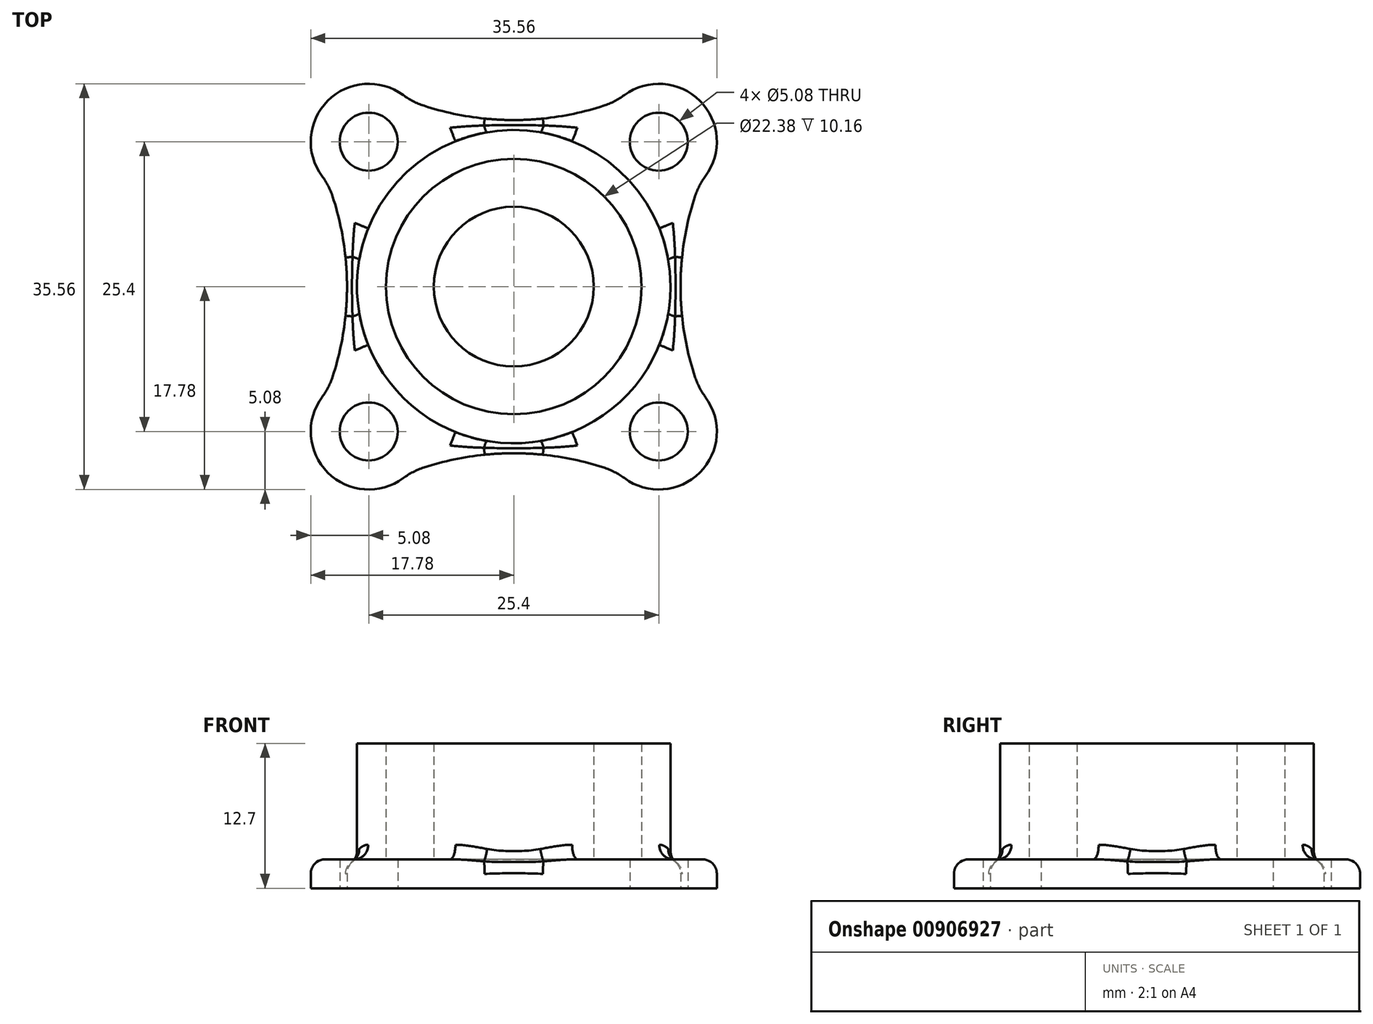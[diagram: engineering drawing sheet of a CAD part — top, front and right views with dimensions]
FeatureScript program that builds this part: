
annotation { "Feature Type Name" : "Feature", "Feature Type Description" : "" }
export const myFeature = defineFeature(function(context is Context, id is Id, definition is map)
    precondition{}
    {
        {
            var Q0;
            Q0=qCreatedBy(makeId("Top.planeOp"),FACE);
            var sketch = newSketch(context, id + "F0", { "sketchPlane" : qUnion([Q0])});
            skCircle(sketch, "E0", {"center": v(0, 0) * mm, "radius": 7 * mm});
            skCircle(sketch, "E1", {"center": v(0, 0) * mm, "radius": 11.2 * mm});
            skCircle(sketch, "E2", {"center": v(0, 0) * mm, "radius": 13.73 * mm});
            skCircle(sketch, "E3", {"center": v(-12.7, 12.7) * mm, "radius": 2.54 * mm});
            skArc(sketch, "E4", {"start": v(-16.79, 9.68) * mm, "mid": v(-16.3, 16.3) * mm, "end": v(-9.68, 16.79) * mm});
            skLineSegment(sketch, "E5", {"start": v(-9.1, 16.3) * mm, "end": v(-16.3, 9.1) * mm, "construction": true});
            skLineSegment(sketch, "E6", {"start": v(-12.7, 12.7) * mm, "end": v(-8.47, 12.7) * mm, "construction": true});
            skArc(sketch, "E7", {"start": v(-15.85, 7.87) * mm, "mid": v(-14.92, 3.99) * mm, "end": v(-14.6, 0) * mm});
            skPoint(sketch, "E8.visualSharp", {"position": v(-16.3, 9.1) * mm});
            skArc(sketch, "E8.filletArc", {"start": v(-15.85, 7.87) * mm, "mid": v(-16.25, 8.81) * mm, "end": v(-16.79, 9.68) * mm});
            skLineSegment(sketch, "E9", {"start": v(-12.7, 12.7) * mm, "end": v(0, 0) * mm, "construction": true});
            skArc(sketch, "E10.MirrorCS", {"start": v(-7.87, 15.85) * mm, "mid": v(-3.99, 14.92) * mm, "end": v(0, 14.6) * mm});
            skArc(sketch, "E11.MirrorCS", {"start": v(-7.87, 15.85) * mm, "mid": v(-8.81, 16.25) * mm, "end": v(-9.68, 16.79) * mm});
            skArc(sketch, "E12.1.0", {"start": v(-15.85, -7.87) * mm, "mid": v(-14.92, -3.99) * mm, "end": v(-14.6, 0) * mm});
            skArc(sketch, "E12.1.1", {"start": v(-15.85, -7.87) * mm, "mid": v(-16.25, -8.81) * mm, "end": v(-16.79, -9.68) * mm});
            skArc(sketch, "E12.1.2", {"start": v(-9.68, -16.79) * mm, "mid": v(-16.3, -16.3) * mm, "end": v(-16.79, -9.68) * mm});
            skArc(sketch, "E12.1.3", {"start": v(-7.87, -15.85) * mm, "mid": v(-8.81, -16.25) * mm, "end": v(-9.68, -16.79) * mm});
            skArc(sketch, "E12.1.4", {"start": v(-7.87, -15.85) * mm, "mid": v(-3.99, -14.92) * mm, "end": v(0, -14.6) * mm});
            skCircle(sketch, "E12.1.5", {"center": v(-12.7, -12.7) * mm, "radius": 2.54 * mm});
            skArc(sketch, "E12.2.0", {"start": v(7.87, -15.85) * mm, "mid": v(3.99, -14.92) * mm, "end": v(0, -14.6) * mm});
            skArc(sketch, "E12.2.1", {"start": v(7.87, -15.85) * mm, "mid": v(8.81, -16.25) * mm, "end": v(9.68, -16.79) * mm});
            skArc(sketch, "E12.2.2", {"start": v(16.79, -9.68) * mm, "mid": v(16.3, -16.3) * mm, "end": v(9.68, -16.79) * mm});
            skArc(sketch, "E12.2.3", {"start": v(15.85, -7.87) * mm, "mid": v(16.25, -8.81) * mm, "end": v(16.79, -9.68) * mm});
            skArc(sketch, "E12.2.4", {"start": v(15.85, -7.87) * mm, "mid": v(14.92, -3.99) * mm, "end": v(14.6, 0) * mm});
            skCircle(sketch, "E12.2.5", {"center": v(12.7, -12.7) * mm, "radius": 2.54 * mm});
            skArc(sketch, "E12.3.0", {"start": v(15.85, 7.87) * mm, "mid": v(14.92, 3.99) * mm, "end": v(14.6, 0) * mm});
            skArc(sketch, "E12.3.1", {"start": v(15.85, 7.87) * mm, "mid": v(16.25, 8.81) * mm, "end": v(16.79, 9.68) * mm});
            skArc(sketch, "E12.3.2", {"start": v(9.68, 16.79) * mm, "mid": v(16.3, 16.3) * mm, "end": v(16.79, 9.68) * mm});
            skArc(sketch, "E12.3.3", {"start": v(7.87, 15.85) * mm, "mid": v(8.81, 16.25) * mm, "end": v(9.68, 16.79) * mm});
            skArc(sketch, "E12.3.4", {"start": v(7.87, 15.85) * mm, "mid": v(3.99, 14.92) * mm, "end": v(0, 14.6) * mm});
            skCircle(sketch, "E12.3.5", {"center": v(12.7, 12.7) * mm, "radius": 2.54 * mm});
            skSolve(sketch);
        }
        {
            var Q0;
            Q0=makeQuery(id+"F0.imprint","IMPRINT",FACE,{"disambiguationData":[TD([[makeQuery(id+"F0.imprint","IMPRINT",EDGE,{"derivedFrom":sQuery(id+"F0.wireOp",EDGE,"E2")}),-1.0]])]});
            var Q1;
            Q1=makeQuery(id+"F0.imprint","IMPRINT",FACE,{"disambiguationData":[TD([[makeQuery(id+"F0.imprint","IMPRINT",EDGE,{"derivedFrom":sQuery(id+"F0.wireOp",EDGE,"E1")}),-1.0]])]});
            var Q2;
            Q2=makeQuery(id+"F0.imprint","IMPRINT",FACE,{"disambiguationData":[TD([[makeQuery(id+"F0.imprint","IMPRINT",EDGE,{"derivedFrom":sQuery(id+"F0.wireOp",EDGE,"E0")}),-1.0]])]});
            extrude(context, id + "F1", {"entities" : qUnion([Q0, Q1, Q2]), "depth" : 2.54 * mm, "offsetDistance" : 25.4 * mm});
        }
        {
            var Q0;
            Q0=makeQuery(id+"F0.imprint","IMPRINT",FACE,{"disambiguationData":[TD([[makeQuery(id+"F0.imprint","IMPRINT",EDGE,{"derivedFrom":sQuery(id+"F0.wireOp",EDGE,"E1")}),-1.0]])]});
            var Q1;
            Q1=makeQuery(id+"F0.imprint","IMPRINT",FACE,{"disambiguationData":[TD([[makeQuery(id+"F0.imprint","IMPRINT",EDGE,{"derivedFrom":sQuery(id+"F0.wireOp",EDGE,"E0")}),1.0]])]});
            extrude(context, id + "F2", {"entities" : qUnion([Q0, Q1]), "operationType" : NewBodyOperationType.ADD, "depth" : 12.7 * mm, "offsetDistance" : 25.4 * mm});
        }
        {
            var Q0;
            Q0=makeQuery(id+"F1.opExtrude","CAP_EDGE",EDGE,{"disambiguationData":[OSD([sQuery(id+"F0.wireOp",EDGE,"E4")])],"isStart":false});
            fillet(context, id + "F3", {"entities" : qUnion([Q0]), "radius" : 1.27 * mm, "tangentPropagation" : true, "allowEdgeOverflow" : false});
        }
        {
            var Q0;
            Q0=makeQuery(id+"F2.boolean.opBoolean","INTERSECT",EDGE,{"derivedFrom":[makeQuery(id+"F1.opExtrude","CAP_FACE",FACE,{"disambiguationData":[OSD([sQuery(id+"F0.wireOp",EDGE,"E0"),sQuery(id+"F0.wireOp",EDGE,"E3"),sQuery(id+"F0.wireOp",EDGE,"E4"),sQuery(id+"F0.wireOp",EDGE,"E7"),sQuery(id+"F0.wireOp",EDGE,"E8.filletArc"),sQuery(id+"F0.wireOp",EDGE,"E10.MirrorCS"),sQuery(id+"F0.wireOp",EDGE,"E11.MirrorCS"),sQuery(id+"F0.wireOp",EDGE,"E12.1.0"),sQuery(id+"F0.wireOp",EDGE,"E12.1.1"),sQuery(id+"F0.wireOp",EDGE,"E12.1.2"),sQuery(id+"F0.wireOp",EDGE,"E12.1.3"),sQuery(id+"F0.wireOp",EDGE,"E12.1.4"),sQuery(id+"F0.wireOp",EDGE,"E12.1.5"),sQuery(id+"F0.wireOp",EDGE,"E12.2.0"),sQuery(id+"F0.wireOp",EDGE,"E12.2.1"),sQuery(id+"F0.wireOp",EDGE,"E12.2.2"),sQuery(id+"F0.wireOp",EDGE,"E12.2.3"),sQuery(id+"F0.wireOp",EDGE,"E12.2.4"),sQuery(id+"F0.wireOp",EDGE,"E12.2.5"),sQuery(id+"F0.wireOp",EDGE,"E12.3.0"),sQuery(id+"F0.wireOp",EDGE,"E12.3.1"),sQuery(id+"F0.wireOp",EDGE,"E12.3.2"),sQuery(id+"F0.wireOp",EDGE,"E12.3.3"),sQuery(id+"F0.wireOp",EDGE,"E12.3.4"),sQuery(id+"F0.wireOp",EDGE,"E12.3.5")])],"isStart":false}),makeQuery(id+"F2.opExtrude","SWEPT_FACE",FACE,{"disambiguationData":[OSD([sQuery(id+"F0.wireOp",EDGE,"E2")])]})]});
            fillet(context, id + "F4", {"entities" : qUnion([Q0]), "radius" : 1.27 * mm, "tangentPropagation" : true, "allowEdgeOverflow" : false});
        }
    });
